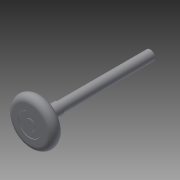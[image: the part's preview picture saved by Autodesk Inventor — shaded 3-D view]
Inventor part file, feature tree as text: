
AUTODESK INVENTOR PART (.ipt)
format: ipt  version: 2015 SP1 (Build 190203100, 203)  size: 131,072 bytes
history: native  units: in
note: dims shown in document units (in); Inventor stores cm internally (conversion verified against a paired STEP export)
features: extrude x5, sketch x5, fillet x1, plane x1, projected_geometry x1
ambient origin geometry x8: Origin, YZ Plane, XZ Plane, XY Plane, X Axis, Y Axis, Z Axis, Center Point
bodies: Solid1 (feature_tree)
feature tree (13):
  extrude  "Extrusion1"  Depth=0.5in
  fillet  "Fillet1"  Radius=0.5in
  extrude  "Extrusion2"  Depth=0.25in
  plane  "Work Plane1"
  extrude  "Extrusion3"  Depth=5.25in
  extrude  "Extrusion4"  Depth=0.475in TaperAngle=0.0deg
  extrude  "Extrusion5"  Depth=0.125in TaperAngle=0.0deg
  sketch  "Sketch1"  dims[d0=2.0in d1=1.0in d2=0.5in d3=0.0in]
  sketch  "Sketch2"  dims[d4=0.25in d5=0.4375in]
  projected_geometry  "Projected Loop1"
  sketch  "Sketch3"  dims[d6=5.25in d7=0.0in d8=0.975in]
  sketch  "Sketch4"  dims[d9=0.453in d10=0.475in d11=0.0in]
  sketch  "Sketch5"  dims[d12=0.5in d13=1.0in d14=0.0in d15=1.5in d16=0.125in d17=0.0in]
